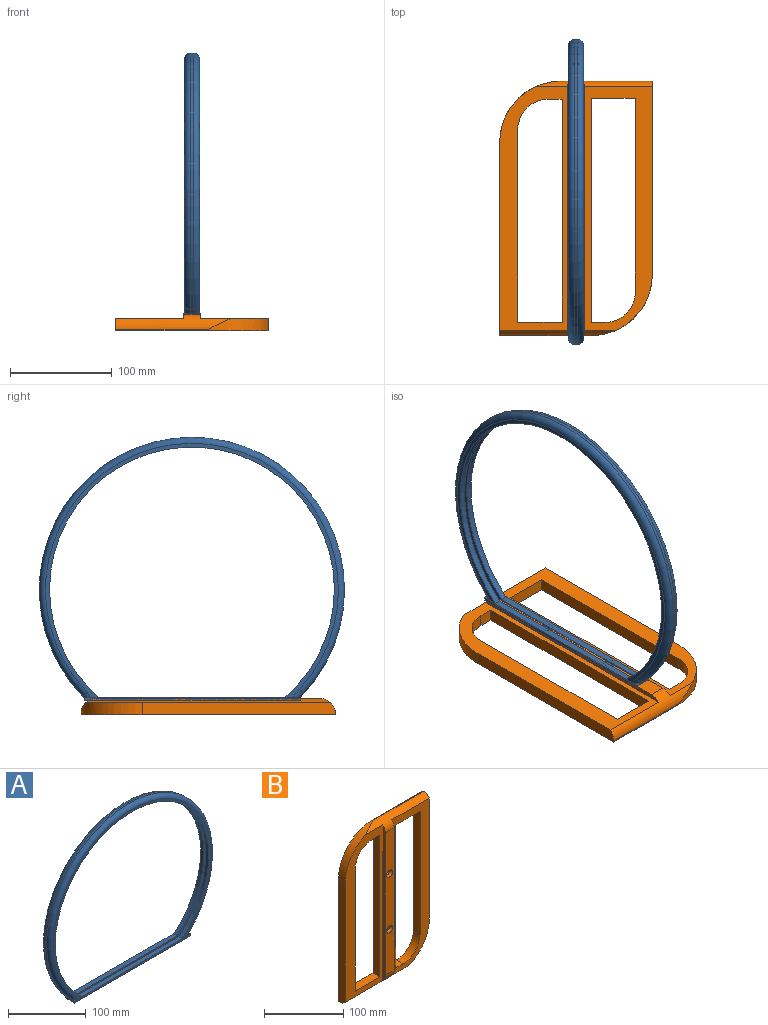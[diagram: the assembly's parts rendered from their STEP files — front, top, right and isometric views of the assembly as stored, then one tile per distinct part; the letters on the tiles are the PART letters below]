
ASSEMBLY  parts=2 mates=1
PART A: 35 faces, bbox 325.1x17.3x276.9 mm
  f0: plane 212x6.5mm, normal (0,0,1), area 1217.2mm2, adj f1,f5,f7,f8,f9,f12,f29,f32
  f1: cylinder r=140mm len=280mm, axis (0,-1,0), area 4083.9mm2, adj f0,f5,f12
  f2: plane 212.4x6.9mm, normal (0,0,1), area 1217.2mm2, adj f4,f6,f7,f9,f10,f13,f25,f28
  f3: cylinder r=150mm len=300mm, axis (0,1,0), area 2098mm2, adj f16,f17,f18,f20,f26,f30
  f4: plane 288x249.8mm, normal (0,-1,0), area 2689.5mm2, adj f2,f6,f25,f26,f28
  f5: plane 288x249.8mm, normal (0,1,0), area 2689.5mm2, adj f0,f1,f29,f30,f32
  f6: cylinder r=140mm len=280mm, axis (0,-1,0), area 4083.9mm2, adj f2,f4,f13
  f7: plane 16x3mm, normal (1,0,0), area 48mm2, adj f0,f2,f8,f10,f11,f20
  f8: plane 212x3mm, normal (0,1,0), area 636mm2, adj f0,f7,f9,f11
  f9: plane 16.13x3.13mm, normal (-1,0,0), area 30.3mm2, adj f0,f2,f8,f10,f11,f19,f28,f32
  f10: plane 212x3mm, normal (0,-1,0), area 636mm2, adj f2,f7,f9,f11
  f11: plane 212x16mm, normal (0,0,-1), area 3195mm2, adj f7,f8,f9,f10,f33,f34
  f12: plane 290x252.68mm, normal (0,-1,0), area 3742.5mm2, adj f0,f1,f14,f15
  f13: plane 290x252.68mm, normal (0,1,0), area 3742.5mm2, adj f2,f6,f14,f15
  f14: cylinder r=145mm len=290mm, axis (0,-1,0), area 2089.2mm2, adj f12,f13,f15,f16
  f15: plane 194.23x3mm, normal (0,0,1), area 582.7mm2, adj f12,f13,f14
  f16: cylinder r=1mm len=9.57mm, axis (1,0,0), area 48.2mm2, adj f3,f14,f17,f18,f19
  f17: cylinder r=3.5mm len=1.38mm, axis (0,-1,0), area 0.3mm2, adj f3,f16,f19,f31
  f18: cylinder r=3.5mm len=1.38mm, axis (0,-1,0), area 0.3mm2, adj f3,f16,f19,f27
  f19: cylinder r=5mm len=3.73mm, axis (0,-1,0), area 8.9mm2, adj f9,f16,f17,f18,f28,f32
  f20: cylinder r=228mm len=3.89mm, axis (0,-1,0), area 15.8mm2, adj f3,f7,f25,f29
  f21: cylinder r=2.5mm len=5mm, axis (0,0,1), area 29.8mm2, adj f22,f34
  f22: plane 5x5mm, normal (0,0,-1), area 19.6mm2, adj f21
  f23: cylinder r=2.5mm len=5mm, axis (0,0,1), area 29.8mm2, adj f24,f33
  f24: plane 5x5mm, normal (0,0,-1), area 19.6mm2, adj f23
  f25: torus R=234mm, axis (0,-1,0), area 68mm2, adj f2,f4,f20,f26
  f26: torus R=144mm, axis (0,-1,0), area 6494.8mm2, adj f3,f4,f25,f27
  f27: bspline ~7.34x4.42mm, area 0.9mm2, adj f18,f26,f28
  f28: torus R=11mm, axis (0,-1,0), area 32.7mm2, adj f2,f4,f9,f19,f27
  f29: torus R=234mm, axis (0,-1,0), area 68mm2, adj f0,f5,f20,f30
  f30: torus R=144mm, axis (0,-1,0), area 6494.8mm2, adj f3,f5,f29,f31
  f31: bspline ~7.34x4.42mm, area 0.9mm2, adj f17,f30,f32
  f32: torus R=11mm, axis (0,-1,0), area 33.5mm2, adj f0,f5,f9,f19,f31
  f33: torus R=5.6mm, axis (0,0,1), area 111mm2, adj f11,f23
  f34: torus R=5.6mm, axis (0,0,1), area 111mm2, adj f11,f21
PART B: 30 faces, bbox 150x16x250 mm
  f0: plane 240.4x67mm, normal (0,-1,0), area 6198.8mm2, adj f1,f2,f3,f4,f6,f7,f16,f19
  f1: cylinder r=30mm len=30mm, axis (0,1,0), area 565.5mm2, adj f0,f2,f16,f18
  f2: plane 13.25x12mm, normal (0,0,1), area 159mm2, adj f0,f1,f3,f18
  f3: plane 220.58x12mm, normal (1,0,0), area 2646.9mm2, adj f0,f2,f4,f18
  f4: plane 43.25x12mm, normal (0,0,-1), area 519mm2, adj f0,f3,f16,f18
  f5: plane 90x1mm, normal (0,0,-1), area 90mm2, adj f6,f14,f18,f23
  f6: cylinder r=60mm len=60mm, axis (0,1,0), area 1004.6mm2, adj f0,f5,f7,f18,f23
  f7: plane 190x12mm, normal (1,0,0), area 2263.7mm2, adj f0,f6,f8,f18,f22
  f8: plane 90x1mm, normal (0,0,1), area 90mm2, adj f7,f9,f18,f22
  f9: cylinder r=60mm len=60mm, axis (0,1,0), area 1004.6mm2, adj f8,f14,f17,f18,f22
  f10: plane 189.22x12mm, normal (1,0,0), area 2270.6mm2, adj f11,f15,f17,f18
  f11: cylinder r=30mm len=30mm, axis (0,1,0), area 565.5mm2, adj f10,f12,f17,f18
  f12: plane 13.68x12mm, normal (0,0,-1), area 164.1mm2, adj f11,f13,f17,f18
  f13: plane 219.22x12mm, normal (-1,0,0), area 2630.6mm2, adj f12,f15,f17,f18
  f14: plane 190x12mm, normal (-1,0,0), area 2263.7mm2, adj f5,f9,f17,f18,f23
  f15: plane 43.68x12mm, normal (0,0,1), area 524.1mm2, adj f10,f13,f17,f18
  f16: plane 190.58x12mm, normal (-1,0,0), area 2286.9mm2, adj f0,f1,f4,f18
  f17: plane 240.4x67mm, normal (0,-1,0), area 6164.2mm2, adj f9,f10,f11,f12,f13,f14,f15,f20
  f18: plane 250x150mm, normal (0,1,0), area 17225.6mm2, adj f1,f2,f3,f4,f5,f6,f7,f8
  f19: plane 240.4x4mm, normal (1,0,0), area 936mm2, adj f0,f21,f22,f23
  f20: plane 240.4x4mm, normal (-1,0,0), area 936mm2, adj f17,f21,f22,f23
  f21: plane 220x16mm, normal (0,-1,0), area 3329.9mm2, adj f19,f20,f22,f23,f28,f29
  f22: cylinder r=15mm len=113.52mm, axis (1,0,0), area 1439.6mm2, adj f0,f7,f8,f9,f17,f19,f20,f21
  f23: cylinder r=15mm len=113.52mm, axis (-1,0,0), area 1439.6mm2, adj f0,f5,f6,f14,f17,f19,f20,f21
  f24: cylinder r=2.5mm len=5mm, axis (0,-1,0), area 62.8mm2, adj f25,f29
  f25: plane 5x5mm, normal (0,-1,0), area 19.6mm2, adj f24
  f26: cylinder r=2.5mm len=5mm, axis (0,-1,0), area 62.8mm2, adj f27,f28
  f27: plane 5x5mm, normal (0,-1,0), area 19.6mm2, adj f26
  f28: cone r=2.5mm half-angle=45deg, axis (0,-1,0), area 106.6mm2, adj f21,f26
  f29: cone r=2.5mm half-angle=45deg, axis (0,-1,0), area 106.6mm2, adj f21,f24
PLACE A rot(axis=(0,0,-1),90deg) t=(294.49,-16.1,-58.79)mm
PLACE B rot(axis=(-1,0,0),90deg) t=(294.49,-16.54,-75.79)mm
MATE fastened A.f21 <-> B.f26  axis (0,0,-1) through (294.49,11.46,-66.79)mm
